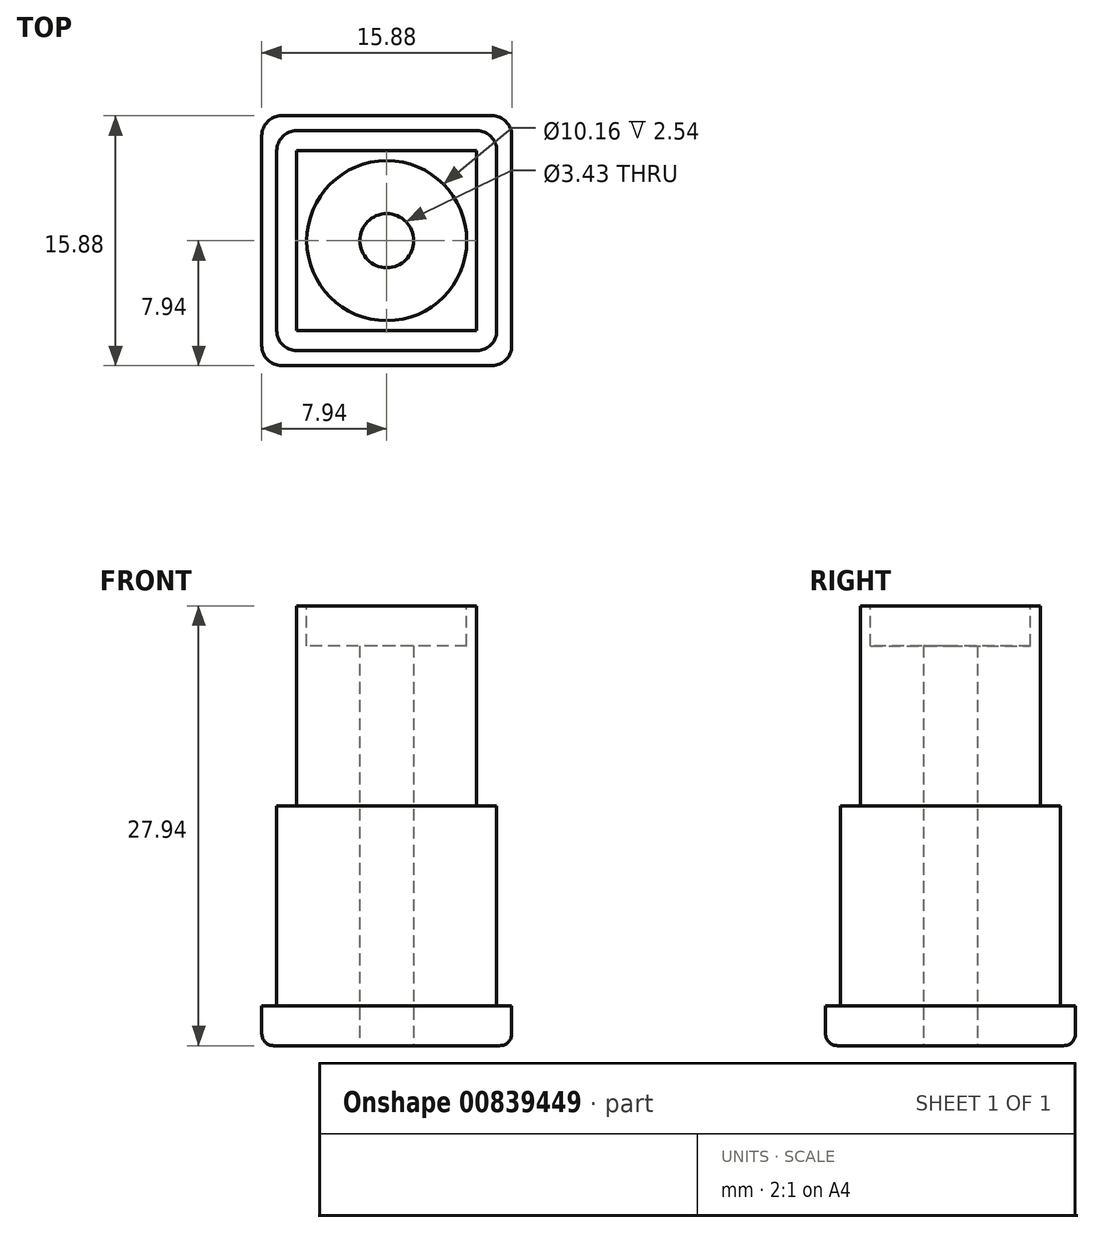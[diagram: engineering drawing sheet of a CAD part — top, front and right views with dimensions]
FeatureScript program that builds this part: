
annotation { "Feature Type Name" : "Feature", "Feature Type Description" : "" }
export const myFeature = defineFeature(function(context is Context, id is Id, definition is map)
    precondition{}
    {
        {
            var Q0;
            Q0=qCreatedBy(makeId("Top.planeOp"),FACE);
            var sketch = newSketch(context, id + "F0", { "sketchPlane" : qUnion([Q0])});
            skLineSegment(sketch, "E0.bottom", {"start": v(6.99, -6.99) * mm, "end": v(-6.99, -6.99) * mm});
            skLineSegment(sketch, "E0.top", {"start": v(6.99, 6.99) * mm, "end": v(-6.99, 6.99) * mm});
            skLineSegment(sketch, "E0.left", {"start": v(6.99, -6.99) * mm, "end": v(6.99, 6.99) * mm});
            skLineSegment(sketch, "E0.right", {"start": v(-6.99, -6.99) * mm, "end": v(-6.99, 6.99) * mm});
            skPoint(sketch, "E0.middle", {"position": v(0, 0) * mm});
            skSolve(sketch);
        }
        {
            var Q0;
            Q0=qSketchRegion(id+"F0",true);
            extrude(context, id + "F1", {"entities" : qUnion([Q0]), "depth" : 25.4 * mm, "offsetDistance" : 25.4 * mm});
        }
        {
            var Q0;
            Q0=makeQuery(id+"F1.opExtrude","CAP_FACE",FACE,{"disambiguationData":[OSD([sQuery(id+"F0.wireOp",EDGE,"E0.bottom"),sQuery(id+"F0.wireOp",EDGE,"E0.top"),sQuery(id+"F0.wireOp",EDGE,"E0.left"),sQuery(id+"F0.wireOp",EDGE,"E0.right")])],"isStart":false});
            var sketch = newSketch(context, id + "F2", { "sketchPlane" : qUnion([Q0])});
            skCircle(sketch, "E1", {"center": v(0, 0) * mm, "radius": 5.08 * mm});
            skSolve(sketch);
        }
        {
            var Q0;
            Q0=qSketchRegion(id+"F2",true);
            extrude(context, id + "F3", {"entities" : qUnion([Q0]), "operationType" : NewBodyOperationType.REMOVE, "oppositeDirection" : true, "depth" : 2.54 * mm, "offsetDistance" : 25.4 * mm});
        }
        {
            var Q0;
            Q0=makeQuery(id+"F1.opExtrude","CAP_FACE",FACE,{"disambiguationData":[OSD([sQuery(id+"F0.wireOp",EDGE,"E0.bottom"),sQuery(id+"F0.wireOp",EDGE,"E0.top"),sQuery(id+"F0.wireOp",EDGE,"E0.left"),sQuery(id+"F0.wireOp",EDGE,"E0.right")])],"isStart":true});
            var sketch = newSketch(context, id + "F4", { "sketchPlane" : qUnion([Q0])});
            skCircle(sketch, "E2", {"center": v(0, 0) * mm, "radius": 1.71 * mm});
            skSolve(sketch);
        }
        {
            var Q0;
            Q0=makeQuery(id+"F1.opExtrude","SWEPT_EDGE",EDGE,{"disambiguationData":[OSD([sQuery(id+"F0.wireOp",EDGE,"E0.top"),sQuery(id+"F0.wireOp",EDGE,"E0.right")])]});
            var Q1;
            Q1=makeQuery(id+"F1.opExtrude","SWEPT_EDGE",EDGE,{"disambiguationData":[OSD([sQuery(id+"F0.wireOp",EDGE,"E0.bottom"),sQuery(id+"F0.wireOp",EDGE,"E0.right")])]});
            var Q2;
            Q2=makeQuery(id+"F1.opExtrude","SWEPT_EDGE",EDGE,{"disambiguationData":[OSD([sQuery(id+"F0.wireOp",EDGE,"E0.top"),sQuery(id+"F0.wireOp",EDGE,"E0.left")])]});
            var Q3;
            Q3=makeQuery(id+"F1.opExtrude","SWEPT_EDGE",EDGE,{"disambiguationData":[OSD([sQuery(id+"F0.wireOp",EDGE,"E0.bottom"),sQuery(id+"F0.wireOp",EDGE,"E0.left")])]});
            fillet(context, id + "F5", {"entities" : qUnion([Q0, Q1, Q2, Q3]), "tangentPropagation" : true, "radius" : 1.27 * mm, "defaultsChanged" : false, "vertexSettings" : [], "allowEdgeOverflow" : false});
        }
        {
            var Q0;
            Q0=makeQuery(id+"F1.opExtrude","CAP_FACE",FACE,{"disambiguationData":[OSD([sQuery(id+"F0.wireOp",EDGE,"E0.bottom"),sQuery(id+"F0.wireOp",EDGE,"E0.top"),sQuery(id+"F0.wireOp",EDGE,"E0.left"),sQuery(id+"F0.wireOp",EDGE,"E0.right")])],"isStart":true});
            var sketch = newSketch(context, id + "F6", { "sketchPlane" : qUnion([Q0])});
            skLineSegment(sketch, "E3.bottom", {"start": v(7.94, -7.94) * mm, "end": v(-7.94, -7.94) * mm});
            skLineSegment(sketch, "E3.top", {"start": v(7.94, 7.94) * mm, "end": v(-7.94, 7.94) * mm});
            skLineSegment(sketch, "E3.left", {"start": v(7.94, -7.94) * mm, "end": v(7.94, 7.94) * mm});
            skLineSegment(sketch, "E3.right", {"start": v(-7.94, -7.94) * mm, "end": v(-7.94, 7.94) * mm});
            skPoint(sketch, "E3.middle", {"position": v(0, 0) * mm});
            skSolve(sketch);
        }
        {
            var Q0;
            Q0=qSketchRegion(id+"F6",true);
            extrude(context, id + "F7", {"entities" : qUnion([Q0]), "operationType" : NewBodyOperationType.ADD, "depth" : 2.54 * mm, "offsetDistance" : 25.4 * mm});
        }
        {
            var Q0;
            Q0=makeQuery(id+"F7.opExtrude","SWEPT_EDGE",EDGE,{"disambiguationData":[OSD([sQuery(id+"F6.wireOp",EDGE,"E3.top"),sQuery(id+"F6.wireOp",EDGE,"E3.left")])]});
            var Q1;
            Q1=makeQuery(id+"F7.opExtrude","SWEPT_EDGE",EDGE,{"disambiguationData":[OSD([sQuery(id+"F6.wireOp",EDGE,"E3.top"),sQuery(id+"F6.wireOp",EDGE,"E3.right")])]});
            var Q2;
            Q2=makeQuery(id+"F7.opExtrude","SWEPT_EDGE",EDGE,{"disambiguationData":[OSD([sQuery(id+"F6.wireOp",EDGE,"E3.bottom"),sQuery(id+"F6.wireOp",EDGE,"E3.right")])]});
            var Q3;
            Q3=makeQuery(id+"F7.opExtrude","SWEPT_EDGE",EDGE,{"disambiguationData":[OSD([sQuery(id+"F6.wireOp",EDGE,"E3.bottom"),sQuery(id+"F6.wireOp",EDGE,"E3.left")])]});
            fillet(context, id + "F8", {"entities" : qUnion([Q0, Q1, Q2, Q3]), "tangentPropagation" : true, "radius" : 1.27 * mm, "defaultsChanged" : true, "vertexSettings" : [], "allowEdgeOverflow" : false});
        }
        {
            var Q0;
            Q0=makeQuery(id+"F7.opExtrude","CAP_EDGE",EDGE,{"disambiguationData":[OSD([sQuery(id+"F6.wireOp",EDGE,"E3.top")])],"isStart":false});
            fillet(context, id + "F9", {"entities" : qUnion([Q0]), "tangentPropagation" : true, "radius" : 0.76 * mm, "defaultsChanged" : true, "vertexSettings" : [], "allowEdgeOverflow" : false});
        }
        {
            var Q0;
            Q0=qSketchRegion(id+"F4",true);
            extrude(context, id + "F10", {"entities" : qUnion([Q0]), "operationType" : NewBodyOperationType.REMOVE, "endBound" : BoundingType.THROUGH_ALL, "oppositeDirection" : true, "depth" : 12.7 * mm, "offsetDistance" : 25.4 * mm, "hasSecondDirection" : true, "secondDirectionBound" : BoundingType.THROUGH_ALL, "secondDirectionOppositeDirection" : false, "secondDirectionDepth" : 25.4 * mm});
        }
        {
            var Q0;
            Q0=makeQuery(id+"F1.opExtrude","CAP_FACE",FACE,{"disambiguationData":[OSD([sQuery(id+"F0.wireOp",EDGE,"E0.bottom"),sQuery(id+"F0.wireOp",EDGE,"E0.top"),sQuery(id+"F0.wireOp",EDGE,"E0.left"),sQuery(id+"F0.wireOp",EDGE,"E0.right")])],"isStart":false});
            var sketch = newSketch(context, id + "F11", { "sketchPlane" : qUnion([Q0])});
            skLineSegment(sketch, "E4.0", {"start": v(5.72, 5.72) * mm, "end": v(-5.72, 5.72) * mm});
            skLineSegment(sketch, "E5.0", {"start": v(-5.72, -5.72) * mm, "end": v(-5.72, 5.72) * mm});
            skLineSegment(sketch, "E6.0", {"start": v(5.72, -5.72) * mm, "end": v(-5.71, -5.72) * mm});
            skLineSegment(sketch, "E7.0", {"start": v(5.72, -5.71) * mm, "end": v(5.72, 5.72) * mm});
            skLineSegment(sketch, "E8.bottom", {"start": v(8.9, -8.89) * mm, "end": v(-8.9, -8.9) * mm});
            skLineSegment(sketch, "E8.top", {"start": v(8.9, 8.9) * mm, "end": v(-8.9, 8.89) * mm});
            skLineSegment(sketch, "E8.left", {"start": v(8.9, -8.89) * mm, "end": v(8.9, 8.9) * mm});
            skLineSegment(sketch, "E8.right", {"start": v(-8.9, -8.9) * mm, "end": v(-8.9, 8.89) * mm});
            skPoint(sketch, "E8.middle", {"position": v(0, 0) * mm});
            skSolve(sketch);
        }
        {
            var Q0;
            Q0 = qSketchRegion(id + "F11", true);
            extrude(context, id + "F12", {"entities" : qUnion([Q0]), "operationType" : NewBodyOperationType.REMOVE, "oppositeDirection" : true, "depth" : 12.7 * mm, "offsetDistance" : 25.4 * mm});
        }
    });
